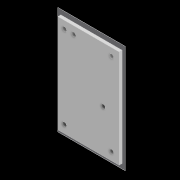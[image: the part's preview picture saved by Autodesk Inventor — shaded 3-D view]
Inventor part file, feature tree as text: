
AUTODESK INVENTOR PART (.ipt)
format: ipt  version: 2020 (Build 240168000, 168)  size: 98,304 bytes
history: native  units: mm
features: sketch x3, hole x2, extrude x1
ambient origin geometry x8: Origin, YZ Plane, XZ Plane, XY Plane, X Axis, Y Axis, Z Axis, Center Point
bodies: Solid1 (feature_tree)
feature tree (6):
  extrude  "Extrusion1"  Depth=79.0mm
  hole  "Hole1"  [1 undecoded]
  hole  "Hole2"  [1 undecoded]
  sketch  "Sketch1"  dims[d0=49.5mm d1=79.0mm]
  sketch  "Sketch2"  dims[d2=2.5mm d3=0.0mm d4=12.777mm]
  sketch  "Sketch3"  dims[d5=6.265mm d6=38.329mm d7=23.774mm d8=3.3mm d9=6.0mm d10=4.0mm d11=2.0mm d12=90.0deg d13=8.0mm d14=20.594885mm d15=6.25mm d16=5.25mm d17=38.0mm d18=72.75mm d19=3.3mm d20=6.0mm d21=4.0mm d22=2.0mm d23=90.0deg d24=8.0mm d25=20.594885mm]
note: 2 required parameter values undecoded (feature->parameter linkage not recoverable at this tier; creation-order binding heuristic only, values carry confidence <= 0.55)
